# Revit family: Valve - PEB Series - 200PEB
name_source: partatom
category: Acessórios do tubo
units: mm (PartAtom-declared; Revit-internal decimal feet)

## family parameters
Com base no plano de trabalho = Não
Compartilhado = Não
Corte com vazios quando carregada = Não
Cota do conector redondo = Utilizar diâmetro
Número OmniClass = 23.60.30.11.14
Sempre na vertical = Sim
Tipo de parte = Normal
Título OmniClass = Pipework Fittings

## types (3) — shared parameters
Anotação Válvula = Sim
Caminho croqui = 11
Diametro Tubo = 5
Material = PVC-U
Material Parafuso = Aço cromado
RainBird: Code = B35213
RainBird: Product Link = https://www.rainbird.com
SupportProjetos: Level of Detail = LOD300
SupportProjetos: Reviw = R01
SupportProjetos: Reviw Date = 10/11/2020
URL = https://www.rainbird.com
zero-valued in all types: Elevação padrão

## per-type parameters (varying)
| type | Descrição | RainBird: Description |
| 200PEB | Valves - PEB Series - 200PEB | Valves - PEB Series - 200PEB |
| 200PESB | Valves - PEB Series - 200PESB | Valves - PEB Series - 200PESB |
| 200PEB-R | Valves - PEB Series - 200PEB-R | Valves - PEB Series - 200PEB-R |

note: column(s) folded — value = type name in every type: Modelo
